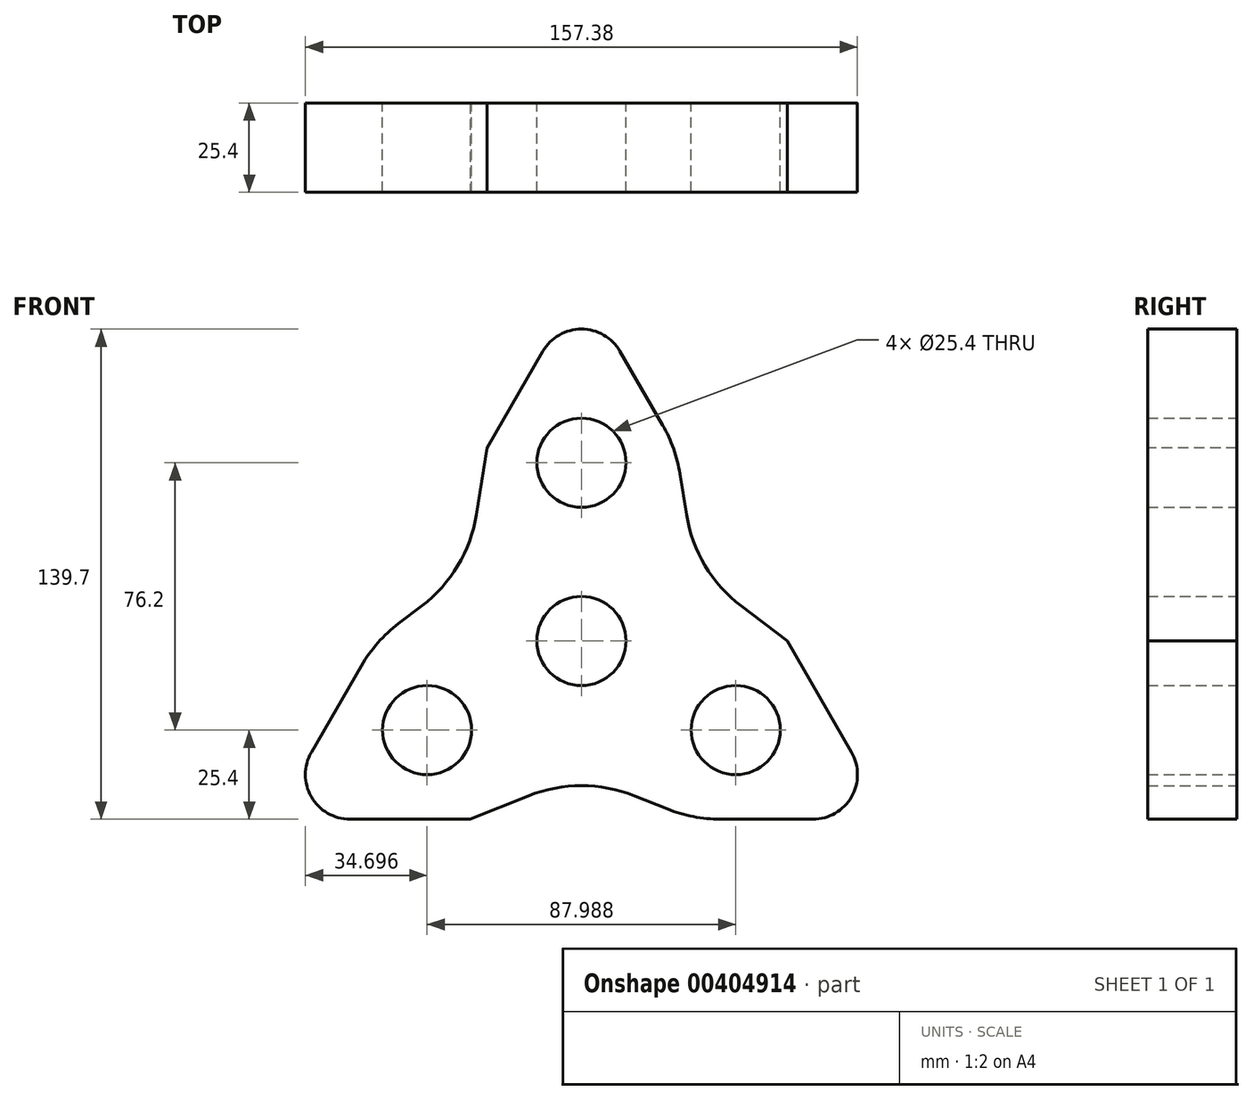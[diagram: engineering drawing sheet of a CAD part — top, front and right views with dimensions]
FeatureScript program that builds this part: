
annotation { "Feature Type Name" : "Feature", "Feature Type Description" : "" }
export const myFeature = defineFeature(function(context is Context, id is Id, definition is map)
    precondition{}
    {
        {
            var Q0;
            Q0=qCreatedBy(makeId("Front.planeOp"),FACE);
            var sketch = newSketch(context, id + "F0", { "sketchPlane" : qUnion([Q0])});
            skCircle(sketch, "E0.cCircle", {"center": v(0, 0) * mm, "radius": 50.8 * mm, "construction": true});
            skLineSegment(sketch, "E0.0", {"start": v(-87.99, -50.8) * mm, "end": v(87.99, -50.8) * mm});
            skLineSegment(sketch, "E0.1", {"start": v(0, 101.6) * mm, "end": v(-87.99, -50.8) * mm});
            skLineSegment(sketch, "E0.2", {"start": v(87.99, -50.8) * mm, "end": v(0, 101.6) * mm});
            skPoint(sketch, "E0.0.midPoint", {"position": v(0, -50.8) * mm});
            skLineSegment(sketch, "E1.0", {"start": v(0, 50.8) * mm, "end": v(-44, -25.4) * mm, "construction": true});
            skLineSegment(sketch, "E1.1", {"start": v(44, -25.4) * mm, "end": v(0, 50.8) * mm, "construction": true});
            skLineSegment(sketch, "E1.2", {"start": v(-44, -25.4) * mm, "end": v(44, -25.4) * mm, "construction": true});
            skCircle(sketch, "E2", {"center": v(0, 50.8) * mm, "radius": 12.7 * mm});
            skCircle(sketch, "E3", {"center": v(44, -25.4) * mm, "radius": 12.7 * mm});
            skCircle(sketch, "E4", {"center": v(-44, -25.4) * mm, "radius": 12.7 * mm});
            skCircle(sketch, "E5", {"center": v(0, 0) * mm, "radius": 12.7 * mm});
            skSolve(sketch);
        }
        {
            var Q0;
            Q0 = qSketchRegion(id + "F0", true);
            extrude(context, id + "F1", {"entities" : qUnion([Q0]), "depth" : 25.4 * mm});
        }
        {
            var Q0;
            Q0=makeQuery(id+"F1.opExtrude","CAP_FACE",FACE,{"disambiguationData":[OSD([sQuery(id+"F0.wireOp",EDGE,"E0.0"),sQuery(id+"F0.wireOp",EDGE,"E0.1"),sQuery(id+"F0.wireOp",EDGE,"E0.2"),sQuery(id+"F0.wireOp",EDGE,"E2"),sQuery(id+"F0.wireOp",EDGE,"E3"),sQuery(id+"F0.wireOp",EDGE,"E4"),sQuery(id+"F0.wireOp",EDGE,"E5")])],"isStart":false});
            var sketch = newSketch(context, id + "F2", { "sketchPlane" : qUnion([Q0])});
            skLineSegment(sketch, "E6", {"start": v(-26.9, 55) * mm, "end": v(-32.53, 19.85) * mm});
            skLineSegment(sketch, "E7", {"start": v(-32.53, 19.85) * mm, "end": v(-58.66, 0) * mm});
            skLineSegment(sketch, "E8", {"start": v(-26.9, 55) * mm, "end": v(-58.66, 0) * mm});
            skLineSegment(sketch, "E9", {"start": v(0, 101.6) * mm, "end": v(0, -50.8) * mm, "construction": true});
            skLineSegment(sketch, "E10.MirrorCS", {"start": v(26.9, 55) * mm, "end": v(32.53, 19.85) * mm});
            skLineSegment(sketch, "E11.MirrorCS", {"start": v(26.9, 55) * mm, "end": v(58.66, 0) * mm});
            skLineSegment(sketch, "E12.MirrorCS", {"start": v(32.53, 19.85) * mm, "end": v(58.66, 0) * mm});
            skLineSegment(sketch, "E13", {"start": v(-31.75, -50.8) * mm, "end": v(0, -38.1) * mm});
            skLineSegment(sketch, "E14", {"start": v(0, -38.1) * mm, "end": v(31.75, -50.8) * mm});
            skLineSegment(sketch, "E15", {"start": v(-31.75, -50.8) * mm, "end": v(31.75, -50.8) * mm});
            skSolve(sketch);
        }
        {
            var Q0;
            Q0 = qSketchRegion(id + "F2", true);
            extrude(context, id + "F3", {"entities" : qUnion([Q0]), "operationType" : NewBodyOperationType.REMOVE, "oppositeDirection" : true, "depth" : 25.4 * mm});
        }
        {
            var Q0;
            Q0=makeQuery(id+"F1.opExtrude","SWEPT_EDGE",EDGE,{"disambiguationData":[OSD([sQuery(id+"F0.wireOp",EDGE,"E0.1"),sQuery(id+"F0.wireOp",EDGE,"E0.2")])]});
            var Q1;
            Q1=makeQuery(id+"F1.opExtrude","SWEPT_EDGE",EDGE,{"disambiguationData":[OSD([sQuery(id+"F0.wireOp",EDGE,"E0.0"),sQuery(id+"F0.wireOp",EDGE,"E0.1")])]});
            var Q2;
            Q2=makeQuery(id+"F1.opExtrude","SWEPT_EDGE",EDGE,{"disambiguationData":[OSD([sQuery(id+"F0.wireOp",EDGE,"E0.0"),sQuery(id+"F0.wireOp",EDGE,"E0.2")])]});
            fillet(context, id + "F4", {"entities" : qUnion([Q0, Q1, Q2]), "radius" : 12.7 * mm, "tangentPropagation" : true, "allowEdgeOverflow" : false});
        }
        {
            var Q0;
            Q0=makeQuery(id+"F3.boolean.opBoolean","COPY",EDGE,{"derivedFrom":makeQuery(id+"F3.opExtrude","SWEPT_EDGE",EDGE,{"disambiguationData":[OSD([sQuery(id+"F0.wireOp",EDGE,"E0.1"),sQuery(id+"F2.wireOp",EDGE,"E6"),sQuery(id+"F2.wireOp",EDGE,"E8")])]})});
            var Q1;
            Q1=makeQuery(id+"F3.boolean.opBoolean","COPY",EDGE,{"derivedFrom":makeQuery(id+"F3.opExtrude","SWEPT_EDGE",EDGE,{"disambiguationData":[OSD([sQuery(id+"F2.wireOp",EDGE,"E6"),sQuery(id+"F2.wireOp",EDGE,"E7")])]})});
            var Q2;
            Q2=makeQuery(id+"F3.boolean.opBoolean","COPY",EDGE,{"derivedFrom":makeQuery(id+"F3.opExtrude","SWEPT_EDGE",EDGE,{"disambiguationData":[OSD([sQuery(id+"F0.wireOp",EDGE,"E0.1"),sQuery(id+"F2.wireOp",EDGE,"E7"),sQuery(id+"F2.wireOp",EDGE,"E8")])]})});
            var Q3;
            Q3=makeQuery(id+"F3.boolean.opBoolean","COPY",EDGE,{"derivedFrom":makeQuery(id+"F3.opExtrude","SWEPT_EDGE",EDGE,{"disambiguationData":[OSD([sQuery(id+"F0.wireOp",EDGE,"E0.2"),sQuery(id+"F2.wireOp",EDGE,"E10.MirrorCS"),sQuery(id+"F2.wireOp",EDGE,"E11.MirrorCS")])]})});
            var Q4;
            Q4=makeQuery(id+"F3.boolean.opBoolean","COPY",EDGE,{"derivedFrom":makeQuery(id+"F3.opExtrude","SWEPT_EDGE",EDGE,{"disambiguationData":[OSD([sQuery(id+"F2.wireOp",EDGE,"E10.MirrorCS"),sQuery(id+"F2.wireOp",EDGE,"E12.MirrorCS")])]})});
            var Q5;
            Q5=makeQuery(id+"F3.boolean.opBoolean","COPY",EDGE,{"derivedFrom":makeQuery(id+"F3.opExtrude","SWEPT_EDGE",EDGE,{"disambiguationData":[OSD([sQuery(id+"F0.wireOp",EDGE,"E0.2"),sQuery(id+"F2.wireOp",EDGE,"E11.MirrorCS"),sQuery(id+"F2.wireOp",EDGE,"E12.MirrorCS")])]})});
            var Q6;
            Q6=makeQuery(id+"F3.boolean.opBoolean","COPY",EDGE,{"derivedFrom":makeQuery(id+"F3.opExtrude","SWEPT_EDGE",EDGE,{"disambiguationData":[OSD([sQuery(id+"F0.wireOp",EDGE,"E0.0"),sQuery(id+"F2.wireOp",EDGE,"E14"),sQuery(id+"F2.wireOp",EDGE,"E15")])]})});
            var Q7;
            Q7=makeQuery(id+"F3.boolean.opBoolean","COPY",EDGE,{"derivedFrom":makeQuery(id+"F3.opExtrude","SWEPT_EDGE",EDGE,{"disambiguationData":[OSD([sQuery(id+"F2.wireOp",EDGE,"E13"),sQuery(id+"F2.wireOp",EDGE,"E14")])]})});
            var Q8;
            Q8=makeQuery(id+"F3.boolean.opBoolean","COPY",EDGE,{"derivedFrom":makeQuery(id+"F3.opExtrude","SWEPT_EDGE",EDGE,{"disambiguationData":[OSD([sQuery(id+"F0.wireOp",EDGE,"E0.0"),sQuery(id+"F2.wireOp",EDGE,"E13"),sQuery(id+"F2.wireOp",EDGE,"E15")])]})});
            fillet(context, id + "F5", {"entities" : qUnion([Q0, Q1, Q2, Q3, Q4, Q5, Q6, Q7, Q8]), "radius" : 40.64 * mm, "tangentPropagation" : true, "allowEdgeOverflow" : false});
        }
    });
